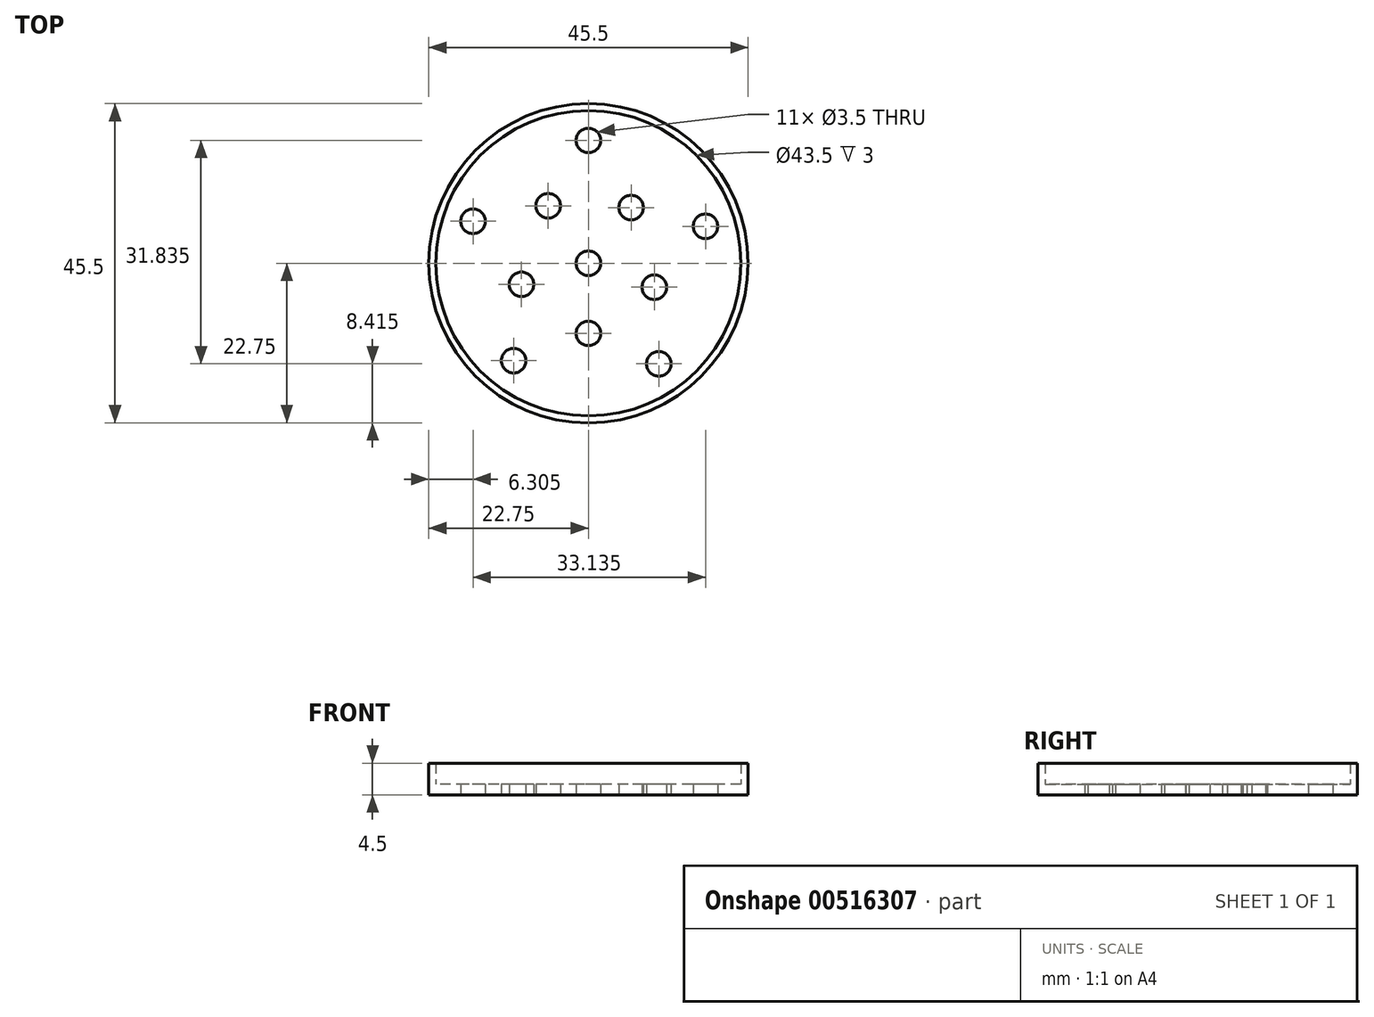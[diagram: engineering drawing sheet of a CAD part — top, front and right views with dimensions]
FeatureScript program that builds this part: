
annotation { "Feature Type Name" : "Feature", "Feature Type Description" : "" }
export const myFeature = defineFeature(function(context is Context, id is Id, definition is map)
    precondition{}
    {
        {
            var Q0;
            Q0=qCreatedBy(makeId("Top.planeOp"),FACE);
            var sketch = newSketch(context, id + "F0", { "sketchPlane" : qUnion([Q0])});
            skCircle(sketch, "E0", {"center": v(0, 0) * mm, "radius": 22.75 * mm});
            skCircle(sketch, "E1", {"center": v(0, 17.5) * mm, "radius": 1.75 * mm});
            skCircle(sketch, "E2", {"center": v(0, 0) * mm, "radius": 1.75 * mm});
            skCircle(sketch, "E3", {"center": v(0, -10) * mm, "radius": 1.75 * mm});
            skCircle(sketch, "E4", {"center": v(0, 0) * mm, "radius": 10 * mm, "construction": true});
            skCircle(sketch, "E5", {"center": v(0, 0) * mm, "radius": 17.5 * mm, "construction": true});
            skCircle(sketch, "E6.1.0", {"center": v(16.7, 5.26) * mm, "radius": 1.75 * mm});
            skCircle(sketch, "E6.1.1", {"center": v(-9.54, -3) * mm, "radius": 1.75 * mm});
            skCircle(sketch, "E6.2.0", {"center": v(10.04, -14.34) * mm, "radius": 1.75 * mm});
            skCircle(sketch, "E6.2.1", {"center": v(-5.74, 8.2) * mm, "radius": 1.75 * mm});
            skCircle(sketch, "E6.3.0", {"center": v(-10.65, -13.88) * mm, "radius": 1.75 * mm});
            skCircle(sketch, "E6.3.1", {"center": v(6.09, 7.93) * mm, "radius": 1.75 * mm});
            skCircle(sketch, "E6.4.0", {"center": v(-16.44, 5.99) * mm, "radius": 1.75 * mm});
            skCircle(sketch, "E6.4.1", {"center": v(9.4, -3.42) * mm, "radius": 1.75 * mm});
            skLineSegment(sketch, "E6.anchor1", {"start": v(0, 0) * mm, "end": v(0, 17.5) * mm, "construction": true});
            skLineSegment(sketch, "E6.anchor2", {"start": v(0, 0) * mm, "end": v(-16.44, 5.99) * mm, "construction": true});
            skSolve(sketch);
        }
        {
            var Q0;
            Q0 = qSketchRegion(id + "F0", true);
            var Q1;
            Q1=makeQuery(id+"F0.imprint","IMPRINT",FACE,{"disambiguationData":[TD([[makeQuery(id+"F0.imprint","IMPRINT",EDGE,{"derivedFrom":sQuery(id+"F0.wireOp",EDGE,"E0")}),1.0]])]});
            extrude(context, id + "F1", {"entities" : qUnion([Q0, Q1]), "depth" : 1.5 * mm, "offsetDistance" : 25 * mm});
        }
        {
            var Q0;
            Q0=makeQuery(id+"F1.opExtrude","CAP_FACE",FACE,{"disambiguationData":[OSD([sQuery(id+"F0.wireOp",EDGE,"E0"),sQuery(id+"F0.wireOp",EDGE,"E1"),sQuery(id+"F0.wireOp",EDGE,"E2"),sQuery(id+"F0.wireOp",EDGE,"TWCooi5L-aTnT-1M0c-O0Y5-KPmZIcpLuNPm"),sQuery(id+"F0.wireOp",EDGE,"bPHiPUte-4hpV-p6p4-N28k-3reJvqDO5KPK"),sQuery(id+"F0.wireOp",EDGE,"M8UWYX2c-IbDI-FY85-8ARU-zRcJiMtr2nGZ"),sQuery(id+"F0.wireOp",EDGE,"E3"),sQuery(id+"F0.wireOp",EDGE,"aenMoB4O-PWK3-OnVd-YDad-c6Gfaia7KRFc"),sQuery(id+"F0.wireOp",EDGE,"FGPCPTK4-8jaq-F3sn-FiUb-EAwH4Sl91hH6"),sQuery(id+"F0.wireOp",EDGE,"dStbVRHB-aOr8-HdHA-yvgj-0EX7lt3nNQs9"),sQuery(id+"F0.wireOp",EDGE,"Xx8VcZl1-S3pS-45Gp-03N9-3TJE0bC2TaLf"),sQuery(id+"F0.wireOp",EDGE,"iy0iu0ur-x6yq-u4wA-1HYK-sW8VEGaAq91q")])],"isStart":false});
            var sketch = newSketch(context, id + "F2", { "sketchPlane" : qUnion([Q0])});
            skCircle(sketch, "E7", {"center": v(0, 0) * mm, "radius": 21.75 * mm});
            skCircle(sketch, "E8", {"center": v(0, 0) * mm, "radius": 22.75 * mm});
            skSolve(sketch);
        }
        {
            var Q0;
            Q0 = qSketchRegion(id + "F2", true);
            extrude(context, id + "F3", {"entities" : qUnion([Q0]), "operationType" : NewBodyOperationType.ADD, "depth" : 3 * mm, "offsetDistance" : 25 * mm});
        }
    });
